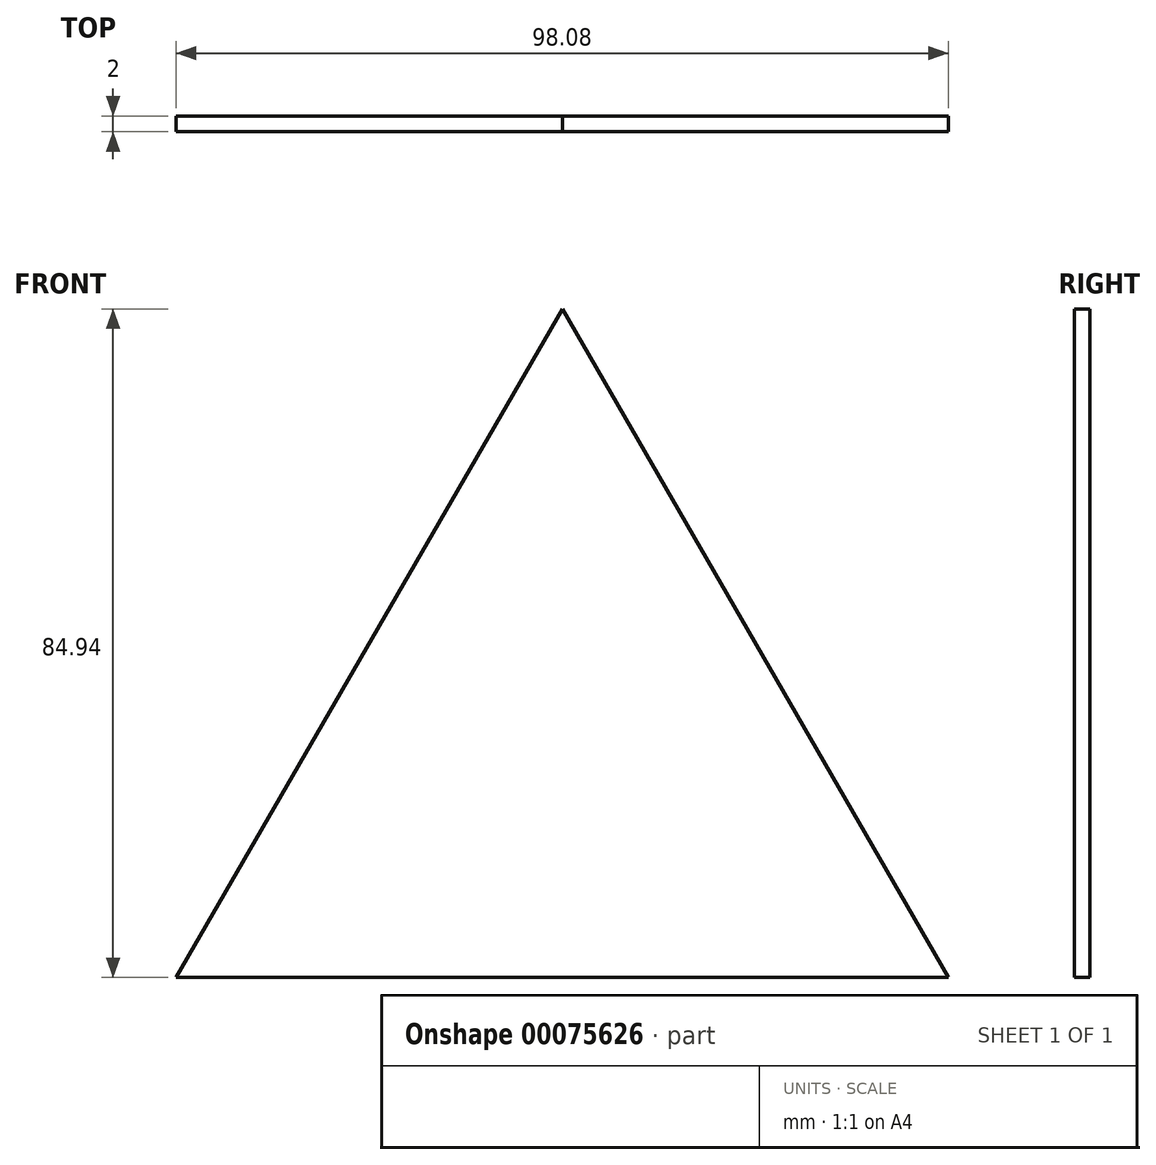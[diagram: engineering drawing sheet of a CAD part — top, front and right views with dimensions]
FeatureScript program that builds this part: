
annotation { "Feature Type Name" : "Feature", "Feature Type Description" : "" }
export const myFeature = defineFeature(function(context is Context, id is Id, definition is map)
    precondition{}
    {
        {
            var Q0;
            Q0=qCreatedBy(makeId("Front.planeOp"),FACE);
            var sketch = newSketch(context, id + "F0", { "sketchPlane" : qUnion([Q0])});
            skLineSegment(sketch, "E0", {"start": v(-408.06, 26.76) * mm, "end": v(-457.1, -58.18) * mm});
            skLineSegment(sketch, "E1", {"start": v(-457.1, -58.18) * mm, "end": v(-359.02, -58.18) * mm});
            skLineSegment(sketch, "E2", {"start": v(-359.02, -58.18) * mm, "end": v(-408.06, 26.76) * mm});
            skLineSegment(sketch, "E3", {"start": v(-457.1, -58.18) * mm, "end": v(-457.1, 26.76) * mm, "construction": true});
            skLineSegment(sketch, "E4", {"start": v(-457.1, 26.76) * mm, "end": v(-408.06, 26.76) * mm, "construction": true});
            skLineSegment(sketch, "E5", {"start": v(-68.1, -18.25) * mm, "end": v(-15.52, -89.51) * mm, "construction": true});
            skLineSegment(sketch, "E6", {"start": v(2.3, -45.83) * mm, "end": v(96.27, 0) * mm, "construction": true});
            skLineSegment(sketch, "E7", {"start": v(-68.1, -18.25) * mm, "end": v(2.3, -45.83) * mm, "construction": true});
            skLineSegment(sketch, "E8", {"start": v(2.3, -45.83) * mm, "end": v(0, 0) * mm, "construction": true});
            skLineSegment(sketch, "E9", {"start": v(0, 0) * mm, "end": v(96.27, 0) * mm, "construction": true});
            skSolve(sketch);
        }
        {
            var Q0;
            Q0 = qSketchRegion(id + "F0", true);
            extrude(context, id + "F1", {"entities" : qUnion([Q0]), "depth" : 2 * mm});
        }
    });
